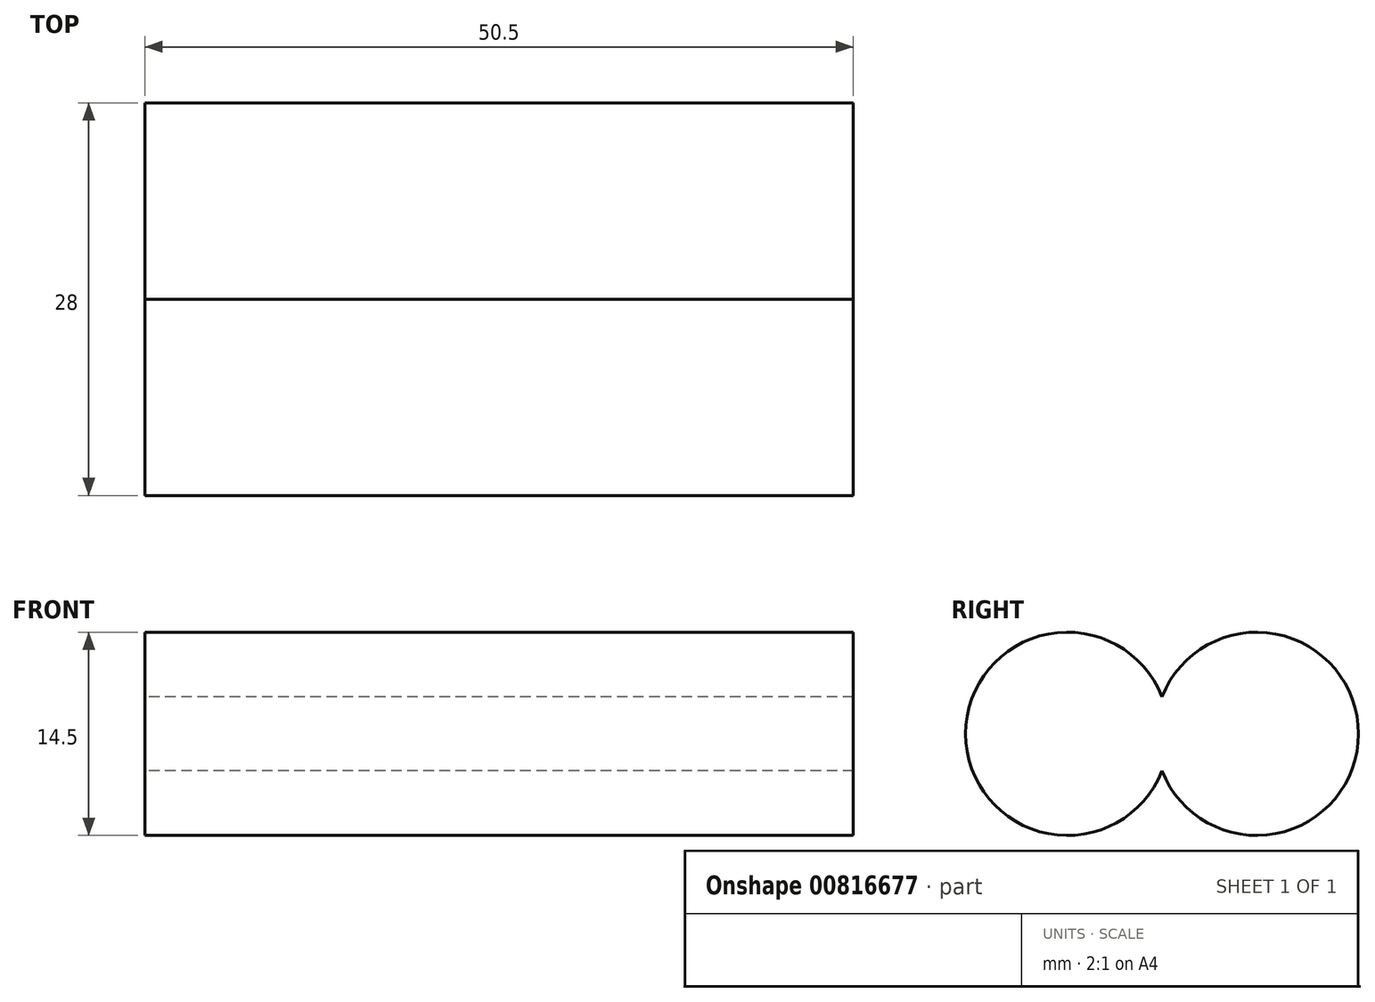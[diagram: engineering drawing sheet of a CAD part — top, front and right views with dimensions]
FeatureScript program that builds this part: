
annotation { "Feature Type Name" : "Feature", "Feature Type Description" : "" }
export const myFeature = defineFeature(function(context is Context, id is Id, definition is map)
    precondition{}
    {
        {
            var Q0;
            Q0=qCreatedBy(makeId("Right.planeOp"),FACE);
            var sketch = newSketch(context, id + "F0", { "sketchPlane" : qUnion([Q0])});
            skLineSegment(sketch, "E0", {"start": v(0, 0) * mm, "end": v(6.75, 0) * mm, "construction": true});
            skCircle(sketch, "E1", {"center": v(6.75, 0) * mm, "radius": 7.25 * mm});
            skSolve(sketch);
        }
        {
            var Q0;
            Q0=makeQuery(id+"F0.imprint","IMPRINT",FACE,{"disambiguationData":[TD([[makeQuery(id+"F0.imprint","IMPRINT",EDGE,{"derivedFrom":sQuery(id+"F0.wireOp",EDGE,"E1")}),1.0]])]});
            extrude(context, id + "F1", {"entities" : qUnion([Q0]), "endBound" : BoundingType.SYMMETRIC, "depth" : 50.5 * mm, "offsetDistance" : 25 * mm});
        }
        {
            var Q0;
            Q0=makeQuery(id+"F1.opExtrude","SWEPT_BODY",BODY,{"disambiguationData":[OSD([sQuery(id+"F0.wireOp",EDGE,"E1")])]});
            var Q1;
            Q1=qCreatedBy(makeId("Front.planeOp"),FACE);
            mirror(context, id + "F2", {"operationType" : NewBodyOperationType.ADD, "entities" : qUnion([Q0]), "mirrorPlane" : qUnion([Q1])});
        }
        {
            var Q0;
            Q0=qCreatedBy(makeId("Top.planeOp"),FACE);
            var sketch = newSketch(context, id + "F3", { "sketchPlane" : qUnion([Q0])});
            skCircle(sketch, "E2", {"center": v(0, 0) * mm, "radius": 11 * mm});
            skCircle(sketch, "E3", {"center": v(0, 0) * mm, "radius": 6.35 * mm});
            skSolve(sketch);
        }
        {
            var Q0;
            Q0=makeQuery(id+"F3.imprint","IMPRINT",FACE,{"disambiguationData":[TD([[makeQuery(id+"F3.imprint","IMPRINT",EDGE,{"derivedFrom":sQuery(id+"F3.wireOp",EDGE,"E2")}),1.0]])]});
            extrude(context, id + "F4", {"entities" : qUnion([Q0]), "endBound" : BoundingType.SYMMETRIC, "depth" : 14.5 * mm, "offsetDistance" : 25 * mm});
        }
        {
            var Q0;
            Q0=makeQuery(id+"F4.opExtrude","SWEPT_BODY",BODY,{"disambiguationData":[OSD([sQuery(id+"F3.wireOp",EDGE,"E2"),sQuery(id+"F3.wireOp",EDGE,"E3")])]});
            deleteBodies(context, id + "F5", {"entities" : qUnion([Q0])});
        }
    });
